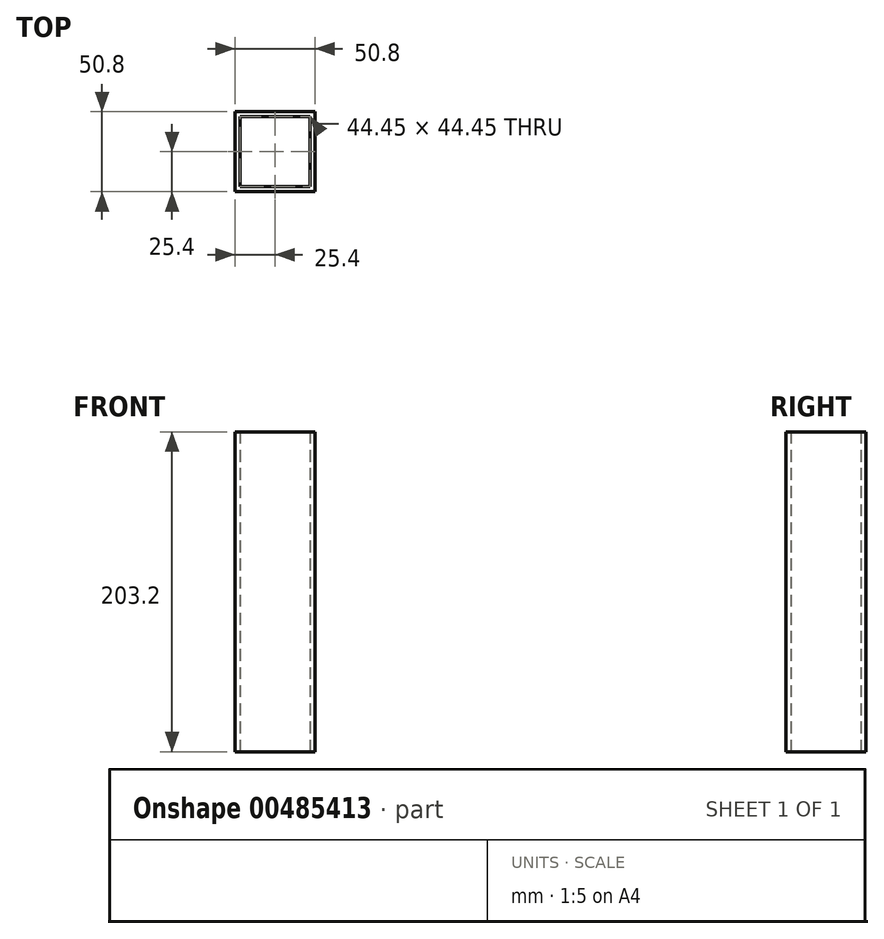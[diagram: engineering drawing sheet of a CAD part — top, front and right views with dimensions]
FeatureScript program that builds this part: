
annotation { "Feature Type Name" : "Feature", "Feature Type Description" : "" }
export const myFeature = defineFeature(function(context is Context, id is Id, definition is map)
    precondition{}
    {
        {
            var Q0;
            Q0=qCreatedBy(makeId("Top.planeOp"),FACE);
            var sketch = newSketch(context, id + "F0", { "sketchPlane" : qUnion([Q0])});
            skLineSegment(sketch, "E0.bottom", {"start": v(25.4, -25.4) * mm, "end": v(-25.4, -25.4) * mm});
            skLineSegment(sketch, "E0.top", {"start": v(25.4, 25.4) * mm, "end": v(-25.4, 25.4) * mm});
            skLineSegment(sketch, "E0.left", {"start": v(25.4, -25.4) * mm, "end": v(25.4, 25.4) * mm});
            skLineSegment(sketch, "E0.right", {"start": v(-25.4, -25.4) * mm, "end": v(-25.4, 25.4) * mm});
            skPoint(sketch, "E0.middle", {"position": v(0, 0) * mm});
            skSolve(sketch);
        }
        {
            var Q0;
            Q0=qCreatedBy(makeId("Top.planeOp"),FACE);
            var sketch = newSketch(context, id + "F1", { "sketchPlane" : qUnion([Q0])});
            skLineSegment(sketch, "E1.bottom", {"start": v(22.23, -22.22) * mm, "end": v(-22.22, -22.23) * mm});
            skLineSegment(sketch, "E1.top", {"start": v(22.22, 22.23) * mm, "end": v(-22.23, 22.22) * mm});
            skLineSegment(sketch, "E1.left", {"start": v(22.23, -22.22) * mm, "end": v(22.22, 22.23) * mm});
            skLineSegment(sketch, "E1.right", {"start": v(-22.22, -22.23) * mm, "end": v(-22.23, 22.22) * mm});
            skPoint(sketch, "E1.middle", {"position": v(0, 0) * mm});
            skSolve(sketch);
        }
        {
            var Q0;
            Q0=makeQuery(id+"F0.imprint","IMPRINT",FACE,{"disambiguationData":[TD([[makeQuery(id+"F0.imprint","IMPRINT",EDGE,{"derivedFrom":sQuery(id+"F0.wireOp",EDGE,"E0.bottom")}),-1.0]])]});
            extrude(context, id + "F2", {"entities" : qUnion([Q0]), "depth" : 203.2 * mm});
        }
        {
            var Q0;
            Q0=makeQuery(id+"F1.imprint","IMPRINT",FACE,{"disambiguationData":[TD([[makeQuery(id+"F1.imprint","IMPRINT",EDGE,{"derivedFrom":sQuery(id+"F1.wireOp",EDGE,"E1.bottom")}),-1.0]])]});
            extrude(context, id + "F3", {"entities" : qUnion([Q0]), "operationType" : NewBodyOperationType.REMOVE, "depth" : 203.2 * mm});
        }
    });
